# Revit family: Shower-Head-Caroma Titan1
name_source: partatom
category: Plumbing Fixtures
revit_build: Autodesk Revit 2013 (Build: 20121003_2115(x64)
units: mm (PartAtom-declared; Revit-internal decimal feet)

## types (2) — shared parameters
Assembly Code = C1030210
CW Connection = No
Description = WELS 3 Star rated, 9L/min
HW Connection = No
Manufacturer = GWA Bathrooms & Kitchens
Material_ANZRS = Metal-Chrome-Caroma
URL = http://www.caroma.com.au
Vent Connection = No
Waste Connection = No
zero-valued in all types: Default Elevation

## per-type parameters (varying)
| type | Large | Length_ANZRS | Model | Small | Type Comments |
| 200mm | No | 200 mm  [stored 0.656168 ft] | 99017SS3A | Yes | Caroma Titan Round Shower Head 200mm |
| 300mm | Yes | 300 mm | 99018SS3A | No | Caroma Titan Round Shower Head 300mm |

note: [stored X ft] marks values corroborated as IEEE doubles in the binary element streams (Revit-internal decimal feet)

## geometry (parser evidence)
native form markers: Blend x4, Sweep x2
no freeform markers — native parametric forms only
